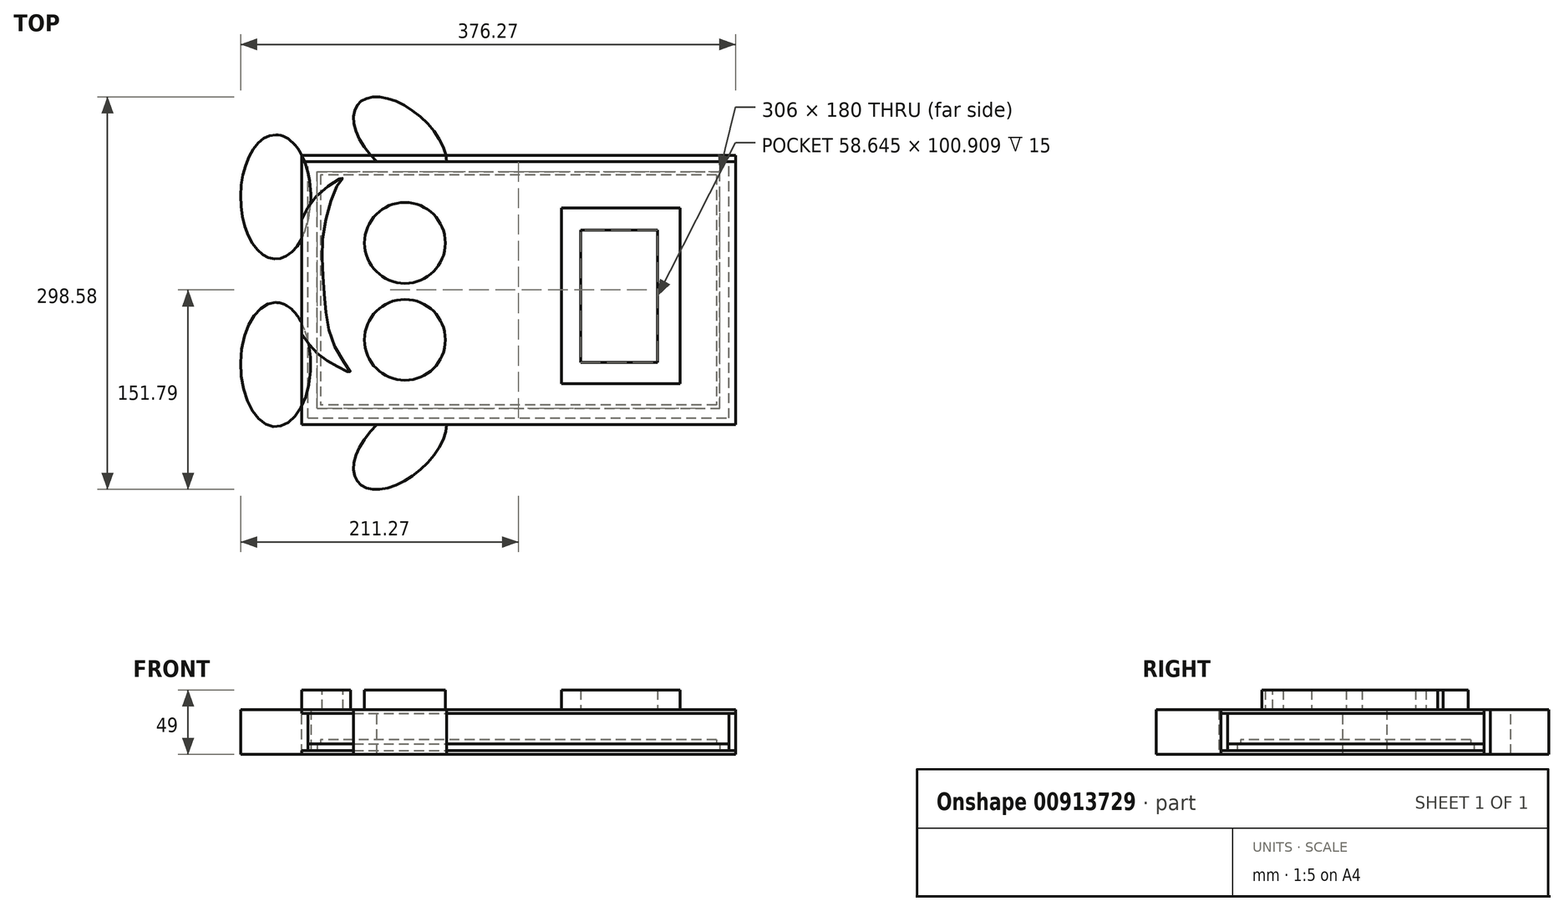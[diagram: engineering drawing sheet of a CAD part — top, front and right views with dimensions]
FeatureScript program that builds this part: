
annotation { "Feature Type Name" : "Feature", "Feature Type Description" : "" }
export const myFeature = defineFeature(function(context is Context, id is Id, definition is map)
    precondition{}
    {
        {
            var Q0;
            Q0=qCreatedBy(makeId("Top.planeOp"),FACE);
            var sketch = newSketch(context, id + "F0", { "sketchPlane" : qUnion([Q0])});
            skLineSegment(sketch, "E0.bottom", {"start": v(0, 0) * mm, "end": v(306, 0) * mm});
            skLineSegment(sketch, "E0.top", {"start": v(0, 180) * mm, "end": v(306, 180) * mm});
            skLineSegment(sketch, "E0.left", {"start": v(0, 0) * mm, "end": v(0, 180) * mm});
            skLineSegment(sketch, "E0.right", {"start": v(306, 0) * mm, "end": v(306, 180) * mm});
            skSolve(sketch);
        }
        {
            var Q0;
            Q0=qSketchRegion(id+"F0",true);
            extrude(context, id + "F1", {"entities" : qUnion([Q0]), "depth" : 5 * mm, "offsetDistance" : 25 * mm});
        }
        {
            var Q0;
            Q0=qCreatedBy(makeId("Top.planeOp"),FACE);
            var sketch = newSketch(context, id + "F2", { "sketchPlane" : qUnion([Q0])});
            skLineSegment(sketch, "E1", {"start": v(0, 0) * mm, "end": v(153, 0) * mm, "construction": true});
            skLineSegment(sketch, "E2", {"start": v(153, 0) * mm, "end": v(153, 90) * mm, "construction": true});
            skLineSegment(sketch, "E3.bottom", {"start": v(-7, -7.5) * mm, "end": v(313, -7.5) * mm});
            skLineSegment(sketch, "E3.top", {"start": v(-7, 187.5) * mm, "end": v(313, 187.5) * mm});
            skLineSegment(sketch, "E3.left", {"start": v(-7, -7.5) * mm, "end": v(-7, 187.5) * mm});
            skLineSegment(sketch, "E3.right", {"start": v(313, -7.5) * mm, "end": v(313, 187.5) * mm});
            skPoint(sketch, "E3.middle", {"position": v(153, 90) * mm});
            skSolve(sketch);
        }
        {
            var Q0;
            Q0=qSketchRegion(id+"F2",true);
            extrude(context, id + "F3", {"entities" : qUnion([Q0]), "depth" : 5 * mm, "offsetDistance" : 25 * mm});
        }
        {
            var Q0;
            Q0=makeQuery(id+"F1.opExtrude","SWEPT_BODY",BODY,{"disambiguationData":[OSD([sQuery(id+"F0.wireOp",EDGE,"E0.bottom"),sQuery(id+"F0.wireOp",EDGE,"E0.top"),sQuery(id+"F0.wireOp",EDGE,"E0.left"),sQuery(id+"F0.wireOp",EDGE,"E0.right")])]});
            var Q1;
            Q1=makeQuery(id+"F3.opExtrude","SWEPT_BODY",BODY,{"disambiguationData":[OSD([sQuery(id+"F2.wireOp",EDGE,"E3.bottom"),sQuery(id+"F2.wireOp",EDGE,"E3.top"),sQuery(id+"F2.wireOp",EDGE,"E3.left"),sQuery(id+"F2.wireOp",EDGE,"E3.right")])]});
            booleanBodies(context, id + "F4", {"operationType" : BooleanOperationType.SUBTRACTION, "tools" : qUnion([Q0]), "targets" : qUnion([Q1]), "keepTools" : true});
        }
        {
            var Q0;
            Q0=makeQuery(id+"F3.opExtrude","CAP_FACE",FACE,{"disambiguationData":[OSD([sQuery(id+"F2.wireOp",EDGE,"E3.bottom"),sQuery(id+"F2.wireOp",EDGE,"E3.top"),sQuery(id+"F2.wireOp",EDGE,"E3.left"),sQuery(id+"F2.wireOp",EDGE,"E3.right")])],"isStart":true});
            var sketch = newSketch(context, id + "F5", { "sketchPlane" : qUnion([Q0])});
            skLineSegment(sketch, "E4.bottom", {"start": v(313, -187.5) * mm, "end": v(-7, -187.5) * mm});
            skLineSegment(sketch, "E4.top", {"start": v(313, 7.5) * mm, "end": v(-7, 7.5) * mm});
            skLineSegment(sketch, "E4.left", {"start": v(313, -187.5) * mm, "end": v(313, 7.5) * mm});
            skLineSegment(sketch, "E4.right", {"start": v(-7, -187.5) * mm, "end": v(-7, 7.5) * mm});
            skLineSegment(sketch, "E5.bottom", {"start": v(-7, 7.5) * mm, "end": v(313, 7.5) * mm});
            skLineSegment(sketch, "E5.top", {"start": v(-7, 12.5) * mm, "end": v(313, 12.5) * mm});
            skLineSegment(sketch, "E5.left", {"start": v(-7, 7.5) * mm, "end": v(-7, 12.5) * mm});
            skLineSegment(sketch, "E5.right", {"start": v(313, 7.5) * mm, "end": v(313, 12.5) * mm});
            skLineSegment(sketch, "E6.bottom", {"start": v(313, 12.5) * mm, "end": v(318, 12.5) * mm});
            skLineSegment(sketch, "E6.top", {"start": v(313, -187.5) * mm, "end": v(318, -187.5) * mm});
            skLineSegment(sketch, "E6.left", {"start": v(313, 12.5) * mm, "end": v(313, -187.5) * mm});
            skLineSegment(sketch, "E6.right", {"start": v(318, 12.5) * mm, "end": v(318, -187.5) * mm});
            skLineSegment(sketch, "E7.bottom", {"start": v(-7, 12.5) * mm, "end": v(-12, 12.5) * mm});
            skLineSegment(sketch, "E7.top", {"start": v(-7, -187.5) * mm, "end": v(-12, -187.5) * mm});
            skLineSegment(sketch, "E7.left", {"start": v(-7, 12.5) * mm, "end": v(-7, -187.5) * mm});
            skLineSegment(sketch, "E7.right", {"start": v(-12, 12.5) * mm, "end": v(-12, -187.5) * mm});
            skSolve(sketch);
        }
        {
            var Q0;
            Q0=qSketchRegion(id+"F5",true);
            extrude(context, id + "F6", {"entities" : qUnion([Q0]), "depth" : 3 * mm, "offsetDistance" : 25 * mm});
        }
        {
            var Q0;
            Q0=makeQuery(id+"F3.opExtrude","CAP_FACE",FACE,{"disambiguationData":[OSD([sQuery(id+"F2.wireOp",EDGE,"E3.bottom"),sQuery(id+"F2.wireOp",EDGE,"E3.top"),sQuery(id+"F2.wireOp",EDGE,"E3.left"),sQuery(id+"F2.wireOp",EDGE,"E3.right")])],"isStart":false});
            var sketch = newSketch(context, id + "F7", { "sketchPlane" : qUnion([Q0])});
            skLineSegment(sketch, "E8.bottom", {"start": v(-7, -7.5) * mm, "end": v(313, -7.5) * mm});
            skLineSegment(sketch, "E8.top", {"start": v(-7, 187.5) * mm, "end": v(313, 187.5) * mm});
            skLineSegment(sketch, "E8.left", {"start": v(-7, -7.5) * mm, "end": v(-7, 187.5) * mm});
            skLineSegment(sketch, "E8.right", {"start": v(313, -7.5) * mm, "end": v(313, 187.5) * mm});
            skLineSegment(sketch, "E9", {"start": v(0, 0) * mm, "end": v(2.5, 0) * mm, "construction": true});
            skLineSegment(sketch, "E10", {"start": v(2.5, 0) * mm, "end": v(2.5, 2.5) * mm, "construction": true});
            skLineSegment(sketch, "E11", {"start": v(306, 180) * mm, "end": v(303.5, 180) * mm, "construction": true});
            skLineSegment(sketch, "E12", {"start": v(303.5, 180) * mm, "end": v(303.5, 177.5) * mm, "construction": true});
            skLineSegment(sketch, "E13.bottom", {"start": v(303.5, 177.5) * mm, "end": v(2.5, 177.5) * mm});
            skLineSegment(sketch, "E13.top", {"start": v(303.5, 2.5) * mm, "end": v(2.5, 2.5) * mm});
            skLineSegment(sketch, "E13.left", {"start": v(303.5, 177.5) * mm, "end": v(303.5, 2.5) * mm});
            skLineSegment(sketch, "E13.right", {"start": v(2.5, 177.5) * mm, "end": v(2.5, 2.5) * mm});
            skSolve(sketch);
        }
        {
            var Q0;
            Q0=qSketchRegion(id+"F7",true);
            extrude(context, id + "F8", {"entities" : qUnion([Q0]), "depth" : 3 * mm, "offsetDistance" : 25 * mm});
        }
        {
            var Q0;
            Q0=makeQuery(id+"F8.opExtrude","CAP_FACE",FACE,{"disambiguationData":[OSD([sQuery(id+"F7.wireOp",EDGE,"E8.bottom"),sQuery(id+"F7.wireOp",EDGE,"E8.top"),sQuery(id+"F7.wireOp",EDGE,"E8.left"),sQuery(id+"F7.wireOp",EDGE,"E8.right"),sQuery(id+"F7.wireOp",EDGE,"E13.bottom"),sQuery(id+"F7.wireOp",EDGE,"E13.top"),sQuery(id+"F7.wireOp",EDGE,"E13.left"),sQuery(id+"F7.wireOp",EDGE,"E13.right")])],"isStart":false});
            var sketch = newSketch(context, id + "F9", { "sketchPlane" : qUnion([Q0])});
            skLineSegment(sketch, "E14.bottom", {"start": v(313, 187.5) * mm, "end": v(-7, 187.5) * mm});
            skLineSegment(sketch, "E14.top", {"start": v(313, -7.5) * mm, "end": v(-7, -7.5) * mm});
            skLineSegment(sketch, "E14.left", {"start": v(313, 187.5) * mm, "end": v(313, -7.5) * mm});
            skLineSegment(sketch, "E14.right", {"start": v(-7, 187.5) * mm, "end": v(-7, -7.5) * mm});
            skSolve(sketch);
        }
        {
            var Q0;
            Q0=qSketchRegion(id+"F9",true);
            extrude(context, id + "F10", {"entities" : qUnion([Q0]), "operationType" : NewBodyOperationType.ADD, "depth" : 20 * mm, "offsetDistance" : 25 * mm});
        }
        {
            var Q0;
            Q0=makeQuery(id+"F10.opExtrude","CAP_FACE",FACE,{"disambiguationData":[OSD([sQuery(id+"F9.wireOp",EDGE,"E14.bottom"),sQuery(id+"F9.wireOp",EDGE,"E14.top"),sQuery(id+"F9.wireOp",EDGE,"E14.left"),sQuery(id+"F9.wireOp",EDGE,"E14.right")])],"isStart":false});
            var sketch = newSketch(context, id + "F11", { "sketchPlane" : qUnion([Q0])});
            skLineSegment(sketch, "E15.bottom", {"start": v(313, -7.5) * mm, "end": v(-7, -7.5) * mm});
            skLineSegment(sketch, "E15.top", {"start": v(313, 187.5) * mm, "end": v(-7, 187.5) * mm});
            skLineSegment(sketch, "E15.left", {"start": v(313, -7.5) * mm, "end": v(313, 187.5) * mm});
            skLineSegment(sketch, "E15.right", {"start": v(-7, -7.5) * mm, "end": v(-7, 187.5) * mm});
            skLineSegment(sketch, "E16.top", {"start": v(313, -12.5) * mm, "end": v(-7, -12.5) * mm});
            skLineSegment(sketch, "E16.left", {"start": v(313, -7.5) * mm, "end": v(313, -12.5) * mm});
            skLineSegment(sketch, "E16.right", {"start": v(-7, -7.5) * mm, "end": v(-7, -12.5) * mm});
            skLineSegment(sketch, "E17.bottom", {"start": v(313, 187.5) * mm, "end": v(318, 187.5) * mm});
            skLineSegment(sketch, "E17.top", {"start": v(313, -12.5) * mm, "end": v(318, -12.5) * mm});
            skLineSegment(sketch, "E17.left", {"start": v(313, 187.5) * mm, "end": v(313, -12.5) * mm});
            skLineSegment(sketch, "E17.right", {"start": v(318, 187.5) * mm, "end": v(318, -12.5) * mm});
            skLineSegment(sketch, "E18.bottom", {"start": v(-7, -12.5) * mm, "end": v(-12, -12.5) * mm});
            skLineSegment(sketch, "E18.top", {"start": v(-7, 187.5) * mm, "end": v(-12, 187.5) * mm});
            skLineSegment(sketch, "E18.left", {"start": v(-7, -12.5) * mm, "end": v(-7, 187.5) * mm});
            skLineSegment(sketch, "E18.right", {"start": v(-12, -12.5) * mm, "end": v(-12, 187.5) * mm});
            skSolve(sketch);
        }
        {
            var Q0;
            Q0=qSketchRegion(id+"F11",true);
            extrude(context, id + "F12", {"entities" : qUnion([Q0]), "depth" : 3 * mm, "offsetDistance" : 25 * mm});
        }
        {
            var Q0;
            Q0=makeQuery(id+"F6.opExtrude","SWEPT_FACE",FACE,{"disambiguationData":[OSD([sQuery(id+"F5.wireOp",EDGE,"E4.bottom"),sQuery(id+"F5.wireOp",EDGE,"E6.top"),sQuery(id+"F5.wireOp",EDGE,"E7.top")])]});
            var sketch = newSketch(context, id + "F13", { "sketchPlane" : qUnion([Q0])});
            skLineSegment(sketch, "E19.bottom", {"start": v(12, -3) * mm, "end": v(-318, -3) * mm});
            skLineSegment(sketch, "E19.top", {"start": v(12, 31) * mm, "end": v(-318, 31) * mm});
            skLineSegment(sketch, "E19.left", {"start": v(12, -3) * mm, "end": v(12, 31) * mm});
            skLineSegment(sketch, "E19.right", {"start": v(-318, -3) * mm, "end": v(-318, 31) * mm});
            skSolve(sketch);
        }
        {
            var Q0;
            Q0=qSketchRegion(id+"F13",true);
            extrude(context, id + "F14", {"entities" : qUnion([Q0]), "depth" : 5 * mm, "offsetDistance" : 25 * mm});
        }
        {
            var Q0;
            Q0=makeQuery(id+"F12.opExtrude","CAP_FACE",FACE,{"disambiguationData":[OSD([sQuery(id+"F11.wireOp",EDGE,"E15.top"),sQuery(id+"F11.wireOp",EDGE,"E16.top"),sQuery(id+"F11.wireOp",EDGE,"E17.bottom"),sQuery(id+"F11.wireOp",EDGE,"E17.top"),sQuery(id+"F11.wireOp",EDGE,"E17.right"),sQuery(id+"F11.wireOp",EDGE,"E18.bottom"),sQuery(id+"F11.wireOp",EDGE,"E18.top"),sQuery(id+"F11.wireOp",EDGE,"E18.right")])],"isStart":false});
            var sketch = newSketch(context, id + "F15", { "sketchPlane" : qUnion([Q0])});
            skLineSegment(sketch, "E20.0", {"start": v(-12, -12.5) * mm, "end": v(318, -12.5) * mm});
            skLineSegment(sketch, "E21.0", {"start": v(-12, 187.5) * mm, "end": v(318, 187.5) * mm});
            skCircle(sketch, "E22", {"center": v(66.62, 125.75) * mm, "radius": 30.74 * mm});
            skCircle(sketch, "E23", {"center": v(66.62, 52.02) * mm, "radius": 30.74 * mm});
            skPoint(sketch, "E24.5.internal.snap0", {"position": v(-12, 87.5) * mm});
            skFitSpline(sketch, "E24", {"points": [v(-12, 143.48) * mm, v(2.44, 164.48) * mm, v(19.57, 175.58) * mm, v(16.47, 171.38) * mm, v(4.62, 133.07) * mm, v(5.33, 87.5) * mm, v(13.83, 45.86) * mm, v(25.3, 27.05) * mm, v(17.45, 30.66) * mm, v(1.36, 40.35) * mm, v(-12, 56.36) * mm], "startDerivative": vector(101.06, 205.6) * mm, "endDerivative": vector(-130.13, 184.99) * mm});
            skLineSegment(sketch, "E25", {"start": v(-12, 143.48) * mm, "end": v(-12, 56.36) * mm});
            skLineSegment(sketch, "E26.bottom", {"start": v(185.7, 152.36) * mm, "end": v(275.8, 152.36) * mm});
            skLineSegment(sketch, "E26.top", {"start": v(185.7, 18.69) * mm, "end": v(275.8, 18.69) * mm});
            skLineSegment(sketch, "E26.left", {"start": v(185.7, 152.36) * mm, "end": v(185.7, 18.69) * mm});
            skLineSegment(sketch, "E26.right", {"start": v(275.8, 152.36) * mm, "end": v(275.8, 18.69) * mm});
            skLineSegment(sketch, "E27.bottom", {"start": v(200.13, 135.65) * mm, "end": v(258.77, 135.65) * mm});
            skLineSegment(sketch, "E27.top", {"start": v(200.13, 34.74) * mm, "end": v(258.77, 34.74) * mm});
            skLineSegment(sketch, "E27.left", {"start": v(200.13, 135.65) * mm, "end": v(200.13, 34.74) * mm});
            skLineSegment(sketch, "E27.right", {"start": v(258.77, 135.65) * mm, "end": v(258.77, 34.74) * mm});
            skSolve(sketch);
        }
        {
            var Q0;
            Q0=makeQuery(id+"F15.imprint","IMPRINT",FACE,{"disambiguationData":[TD([[makeQuery(id+"F15.imprint","IMPRINT",EDGE,{"derivedFrom":sQuery(id+"F15.wireOp",EDGE,"E22")}),1.0]])]});
            var Q1;
            Q1=makeQuery(id+"F15.imprint","IMPRINT",FACE,{"disambiguationData":[TD([[makeQuery(id+"F15.imprint","IMPRINT",EDGE,{"derivedFrom":sQuery(id+"F15.wireOp",EDGE,"E23")}),1.0]])]});
            var Q2;
            Q2 = qSketchRegion(id + "F15", true);
            extrude(context, id + "F16", {"entities" : qUnion([Q0, Q1, Q2]), "operationType" : NewBodyOperationType.ADD, "depth" : 15 * mm, "offsetDistance" : 25 * mm});
        }
        {
            var Q0;
            {var subQ0=sQuery(id+"F11.wireOp",EDGE,"E18.top");var subQ1=sQuery(id+"F11.wireOp",EDGE,"E17.bottom");var subQ2=sQuery(id+"F11.wireOp",EDGE,"E15.top");var subQ3=sQuery(id+"F11.wireOp",EDGE,"E18.bottom");var subQ4=sQuery(id+"F11.wireOp",EDGE,"E17.top");var subQ5=sQuery(id+"F11.wireOp",EDGE,"E16.top");var subQ6=sQuery(id+"F11.wireOp",EDGE,"E17.right");var subQ7=sQuery(id+"F11.wireOp",EDGE,"E18.right");Q0=makeQuery(id+"F16.boolean.opBoolean","SPLIT",FACE,{"disambiguationData":[TD([makeQuery(id+"F12.opExtrude","SWEPT_FACE",FACE,{"disambiguationData":[OSD([subQ6])]})])],"derivedFrom":makeQuery(id+"F12.opExtrude","CAP_FACE",FACE,{"disambiguationData":[OSD([subQ2,subQ5,subQ1,subQ4,subQ6,subQ3,subQ0,subQ7])],"isStart":false})});}
            var sketch = newSketch(context, id + "F17", { "sketchPlane" : qUnion([Q0])});
            skEllipse(sketch, "E28", {"center": v(-31.61, 160.75) * mm, "majorRadius": 26.66 * mm, "minorRadius": 47.26 * mm, "majorAxis": v(1, 0)});
            skLineSegment(sketch, "E29", {"start": v(4.56, 96.97) * mm, "end": v(-71.5, 96.97) * mm, "construction": true});
            skEllipse(sketch, "E30.MirrorC", {"center": v(-31.61, 33.18) * mm, "majorRadius": 26.66 * mm, "minorRadius": 47.26 * mm, "majorAxis": v(1, 0)});
            skEllipse(sketch, "E31", {"center": v(63.04, -28.6) * mm, "majorRadius": 42.36 * mm, "minorRadius": 23.77 * mm, "majorAxis": v(-0.75, -0.66)});
            skLineSegment(sketch, "E32", {"start": v(28.78, 87.5) * mm, "end": v(113.42, 87.5) * mm, "construction": true});
            skEllipse(sketch, "E33.MirrorC", {"center": v(63.04, 203.6) * mm, "majorRadius": 42.36 * mm, "minorRadius": 23.77 * mm, "majorAxis": v(-0.75, 0.66)});
            skSolve(sketch);
        }
        {
            var Q0;
            {var subQ0=sQuery(id+"F17.wireOp",EDGE,"E30.MirrorC");var subQ1=sQuery(id+"F15.wireOp",EDGE,"E24");var subQ2=makeQuery(id+"F16.opExtrude","CAP_EDGE",EDGE,{"disambiguationData":[OSD([subQ1])],"isStart":true});var subQ3=makeQuery(id+"F17.imprint","INTERSECT",VERTEX,{"derivedFrom":[subQ2,subQ0]});Q0=makeQuery(id+"F17.imprint","IMPRINT",FACE,{"disambiguationData":[TD([[makeQuery(id+"F17.imprint","IMPRINT",EDGE,{"disambiguationData":[TD([[subQ3,-1.0]])],"derivedFrom":subQ0}),1.0]])]});}
            var Q1;
            {var subQ0=sQuery(id+"F17.wireOp",EDGE,"E28");var subQ6=sQuery(id+"F15.wireOp",EDGE,"E24");var subQ7=makeQuery(id+"F16.opExtrude","CAP_EDGE",EDGE,{"disambiguationData":[OSD([subQ6])],"isStart":true});var subQ8=makeQuery(id+"F17.imprint","INTERSECT",VERTEX,{"derivedFrom":[subQ7,subQ0]});Q1=makeQuery(id+"F17.imprint","IMPRINT",FACE,{"disambiguationData":[TD([[makeQuery(id+"F17.imprint","IMPRINT",EDGE,{"disambiguationData":[TD([[subQ8,1.0]])],"derivedFrom":subQ0}),1.0]])]});}
            var Q2;
            {var subQ0=sQuery(id+"F17.wireOp",EDGE,"E31");var subQ1=makeQuery(id+"F12.opExtrude","CAP_EDGE",EDGE,{"disambiguationData":[OSD([sQuery(id+"F11.wireOp",EDGE,"E16.top"),sQuery(id+"F11.wireOp",EDGE,"E17.top"),sQuery(id+"F11.wireOp",EDGE,"E18.bottom")])],"isStart":false});var subQ2=makeQuery(id+"F17.imprint","INTERSECT",VERTEX,{"disambiguationData":[OD(0.0)],"derivedFrom":[subQ1,subQ0]});Q2=makeQuery(id+"F17.imprint","IMPRINT",FACE,{"disambiguationData":[TD([[makeQuery(id+"F17.imprint","IMPRINT",EDGE,{"disambiguationData":[TD([[subQ2,1.0]])],"derivedFrom":subQ0}),1.0]])]});}
            var Q3;
            {var subQ0=sQuery(id+"F17.wireOp",EDGE,"E33.MirrorC");var subQ1=makeQuery(id+"F12.opExtrude","CAP_EDGE",EDGE,{"disambiguationData":[OSD([sQuery(id+"F11.wireOp",EDGE,"E15.top"),sQuery(id+"F11.wireOp",EDGE,"E17.bottom"),sQuery(id+"F11.wireOp",EDGE,"E18.top")])],"isStart":false});var subQ2=makeQuery(id+"F17.imprint","INTERSECT",VERTEX,{"disambiguationData":[OD(0.0)],"derivedFrom":[subQ1,subQ0]});Q3=makeQuery(id+"F17.imprint","IMPRINT",FACE,{"disambiguationData":[TD([[makeQuery(id+"F17.imprint","IMPRINT",EDGE,{"disambiguationData":[TD([[subQ2,-1.0]])],"derivedFrom":subQ0}),1.0]])]});}
            var Q4;
            Q4=makeQuery(id+"F6.opExtrude","CAP_FACE",FACE,{"disambiguationData":[OSD([sQuery(id+"F5.wireOp",EDGE,"E4.bottom"),sQuery(id+"F5.wireOp",EDGE,"E5.top"),sQuery(id+"F5.wireOp",EDGE,"E6.bottom"),sQuery(id+"F5.wireOp",EDGE,"E6.top"),sQuery(id+"F5.wireOp",EDGE,"E6.right"),sQuery(id+"F5.wireOp",EDGE,"E7.bottom"),sQuery(id+"F5.wireOp",EDGE,"E7.top"),sQuery(id+"F5.wireOp",EDGE,"E7.right")])],"isStart":false});
            extrude(context, id + "F18", {"entities" : qUnion([Q0, Q1, Q2, Q3]), "endBound" : BoundingType.UP_TO_SURFACE, "oppositeDirection" : true, "depth" : 25 * mm, "endBoundEntityFace" : qUnion([Q4]), "offsetDistance" : 25 * mm});
        }
    });
